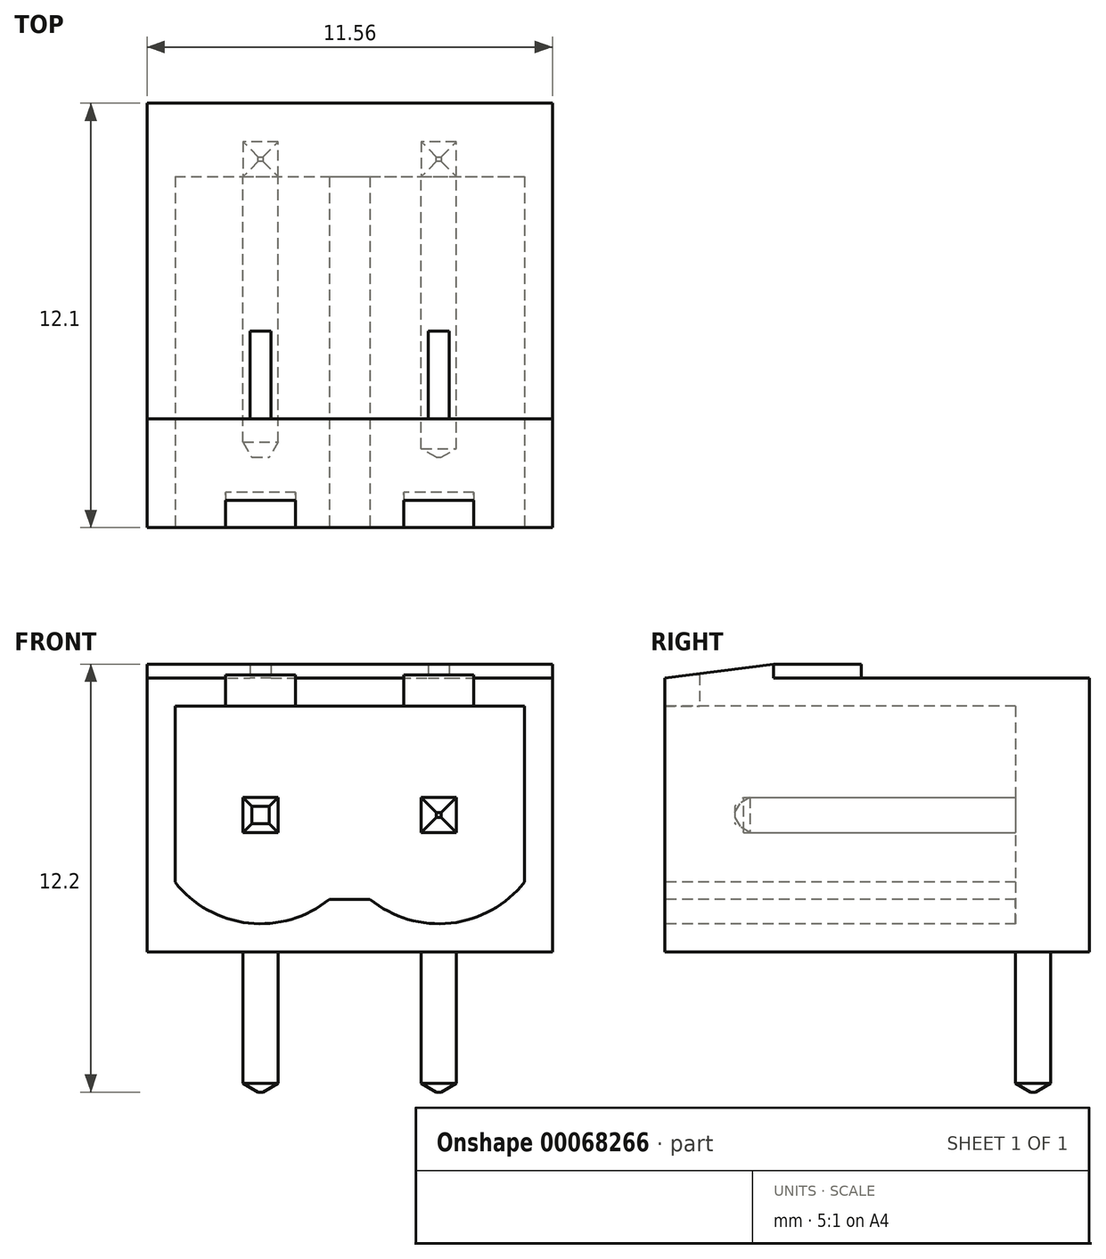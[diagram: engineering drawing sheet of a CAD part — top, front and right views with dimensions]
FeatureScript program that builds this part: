
annotation { "Feature Type Name" : "Feature", "Feature Type Description" : "" }
export const myFeature = defineFeature(function(context is Context, id is Id, definition is map)
    precondition{}
    {
        {
            var Q0;
            Q0=qCreatedBy(makeId("Top.planeOp"),FACE);
            var sketch = newSketch(context, id + "F0", { "sketchPlane" : qUnion([Q0])});
            skLineSegment(sketch, "E0.bottom", {"start": v(-5.78, 6.05) * mm, "end": v(5.78, 6.05) * mm});
            skLineSegment(sketch, "E0.top", {"start": v(-5.78, -6.05) * mm, "end": v(5.78, -6.05) * mm});
            skLineSegment(sketch, "E0.left", {"start": v(-5.78, 6.05) * mm, "end": v(-5.78, -6.05) * mm});
            skLineSegment(sketch, "E0.right", {"start": v(5.78, 6.05) * mm, "end": v(5.78, -6.05) * mm});
            skPoint(sketch, "E0.middle", {"position": v(0, 0) * mm});
            skSolve(sketch);
        }
        {
            var Q0;
            Q0=qSketchRegion(id+"F0",true);
            extrude(context, id + "F1", {"entities" : qUnion([Q0]), "depth" : 8.2 * mm});
        }
        {
            var Q0;
            Q0=makeQuery(id+"F1.opExtrude","SWEPT_FACE",FACE,{"disambiguationData":[OSD([sQuery(id+"F0.wireOp",EDGE,"E0.top")])]});
            var sketch = newSketch(context, id + "F2", { "sketchPlane" : qUnion([Q0])});
            skLineSegment(sketch, "E1.bottom", {"start": v(-4.98, 7) * mm, "end": v(4.98, 7) * mm});
            skLineSegment(sketch, "E1.top", {"start": v(-2.54, 0.8) * mm, "end": v(2.54, 0.8) * mm, "construction": true});
            skLineSegment(sketch, "E1.left", {"start": v(-4.98, 7) * mm, "end": v(-4.98, 1.99) * mm});
            skLineSegment(sketch, "E1.right", {"start": v(4.98, 7) * mm, "end": v(4.98, 1.99) * mm});
            skPoint(sketch, "E1.middle", {"position": v(0, 4.1) * mm});
            skPoint(sketch, "E1.middle.positionSnap0", {"position": v(0, 8.2) * mm});
            skPoint(sketch, "E1.middle.positionSnap1", {"position": v(-5.78, 4.1) * mm});
            skPoint(sketch, "E1.centerSnap0", {"position": v(0, 8.2) * mm});
            skPoint(sketch, "E1.centerSnap1", {"position": v(-5.78, 4.1) * mm});
            skArc(sketch, "E2", {"start": v(-4.98, 1.99) * mm, "mid": v(-2.88, 0.82) * mm, "end": v(-0.58, 1.5) * mm});
            skPoint(sketch, "E2.centerSnap0", {"position": v(-4.98, 3.9) * mm});
            skArc(sketch, "E3", {"start": v(0.58, 1.5) * mm, "mid": v(2.88, 0.82) * mm, "end": v(4.98, 1.99) * mm});
            skPoint(sketch, "E3.centerSnap0", {"position": v(4.98, 3.9) * mm});
            skLineSegment(sketch, "E4", {"start": v(-2.54, 3.9) * mm, "end": v(2.54, 3.9) * mm, "construction": true});
            skLineSegment(sketch, "E5", {"start": v(0, 3.9) * mm, "end": v(0, 7) * mm, "construction": true});
            skPoint(sketch, "E6.orphan", {"position": v(-4.98, 0.8) * mm});
            skPoint(sketch, "E7.orphan", {"position": v(4.98, 0.8) * mm});
            skLineSegment(sketch, "E8", {"start": v(-0.58, 1.5) * mm, "end": v(0.58, 1.5) * mm});
            skSolve(sketch);
        }
        {
            var Q0;
            Q0=qSketchRegion(id+"F2",true);
            extrude(context, id + "F3", {"entities" : qUnion([Q0]), "operationType" : NewBodyOperationType.REMOVE, "oppositeDirection" : true, "depth" : 10 * mm});
        }
        {
            var Q0;
            Q0=makeQuery(id+"F3.boolean.opBoolean","COPY",FACE,{"derivedFrom":makeQuery(id+"F3.opExtrude","CAP_FACE",FACE,{"disambiguationData":[OSD([sQuery(id+"F2.wireOp",EDGE,"E1.bottom"),sQuery(id+"F2.wireOp",EDGE,"E1.left"),sQuery(id+"F2.wireOp",EDGE,"E1.right"),sQuery(id+"F2.wireOp",EDGE,"E2"),sQuery(id+"F2.wireOp",EDGE,"E3"),sQuery(id+"F2.wireOp",EDGE,"E8")])],"isStart":false})});
            var sketch = newSketch(context, id + "F4", { "sketchPlane" : qUnion([Q0])});
            skLineSegment(sketch, "E9.bottom", {"start": v(-2.04, 4.4) * mm, "end": v(-3.04, 4.4) * mm});
            skLineSegment(sketch, "E9.top", {"start": v(-2.04, 3.4) * mm, "end": v(-3.04, 3.4) * mm});
            skLineSegment(sketch, "E9.left", {"start": v(-2.04, 4.4) * mm, "end": v(-2.04, 3.4) * mm});
            skLineSegment(sketch, "E9.right", {"start": v(-3.04, 4.4) * mm, "end": v(-3.04, 3.4) * mm});
            skPoint(sketch, "E9.middle", {"position": v(-2.54, 3.9) * mm});
            skLineSegment(sketch, "E10.bottom", {"start": v(2.04, 4.4) * mm, "end": v(3.04, 4.4) * mm});
            skLineSegment(sketch, "E10.top", {"start": v(2.04, 3.4) * mm, "end": v(3.04, 3.4) * mm});
            skLineSegment(sketch, "E10.left", {"start": v(2.04, 4.4) * mm, "end": v(2.04, 3.4) * mm});
            skLineSegment(sketch, "E10.right", {"start": v(3.04, 4.4) * mm, "end": v(3.04, 3.4) * mm});
            skPoint(sketch, "E10.middle", {"position": v(2.54, 3.9) * mm});
            skSolve(sketch);
        }
        {
            var Q0;
            Q0=qSketchRegion(id+"F4",true);
            extrude(context, id + "F5", {"entities" : qUnion([Q0]), "depth" : 8 * mm});
        }
        {
            var Q0;
            Q0=makeQuery(id+"F1.opExtrude","CAP_FACE",FACE,{"disambiguationData":[OSD([sQuery(id+"F0.wireOp",EDGE,"E0.bottom"),sQuery(id+"F0.wireOp",EDGE,"E0.top"),sQuery(id+"F0.wireOp",EDGE,"E0.left"),sQuery(id+"F0.wireOp",EDGE,"E0.right")])],"isStart":true});
            var sketch = newSketch(context, id + "F6", { "sketchPlane" : qUnion([Q0])});
            skPoint(sketch, "E11.centerSnap0", {"position": v(-5.78, 0) * mm});
            skPoint(sketch, "E12.centerSnap0", {"position": v(5.78, 0) * mm});
            skLineSegment(sketch, "E13", {"start": v(-2.54, -4.45) * mm, "end": v(2.54, -4.45) * mm, "construction": true});
            skLineSegment(sketch, "E14", {"start": v(0, -4.45) * mm, "end": v(0, -6.05) * mm, "construction": true});
            skLineSegment(sketch, "E15.bottom", {"start": v(-3.04, -3.95) * mm, "end": v(-2.04, -3.95) * mm});
            skLineSegment(sketch, "E15.top", {"start": v(-3.04, -4.95) * mm, "end": v(-2.04, -4.95) * mm});
            skLineSegment(sketch, "E15.left", {"start": v(-3.04, -3.95) * mm, "end": v(-3.04, -4.95) * mm});
            skLineSegment(sketch, "E15.right", {"start": v(-2.04, -3.95) * mm, "end": v(-2.04, -4.95) * mm});
            skPoint(sketch, "E15.middle", {"position": v(-2.54, -4.45) * mm});
            skLineSegment(sketch, "E16.bottom", {"start": v(2.04, -3.95) * mm, "end": v(3.04, -3.95) * mm});
            skLineSegment(sketch, "E16.top", {"start": v(2.04, -4.95) * mm, "end": v(3.04, -4.95) * mm});
            skLineSegment(sketch, "E16.left", {"start": v(2.04, -3.95) * mm, "end": v(2.04, -4.95) * mm});
            skLineSegment(sketch, "E16.right", {"start": v(3.04, -3.95) * mm, "end": v(3.04, -4.95) * mm});
            skPoint(sketch, "E16.middle", {"position": v(2.54, -4.45) * mm});
            skSolve(sketch);
        }
        {
            var Q0;
            Q0=qSketchRegion(id+"F6",true);
            extrude(context, id + "F7", {"entities" : qUnion([Q0]), "depth" : 4 * mm});
        }
        {
            var Q0;
            Q0=makeQuery(id+"F1.opExtrude","SWEPT_FACE",FACE,{"disambiguationData":[OSD([sQuery(id+"F0.wireOp",EDGE,"E0.right")])]});
            var sketch = newSketch(context, id + "F8", { "sketchPlane" : qUnion([Q0])});
            skLineSegment(sketch, "E17.bottom", {"start": v(6.05, 8.2) * mm, "end": v(-2.95, 8.2) * mm});
            skLineSegment(sketch, "E17.top", {"start": v(6.05, 7.8) * mm, "end": v(-2.95, 7.8) * mm});
            skLineSegment(sketch, "E17.left", {"start": v(6.05, 8.2) * mm, "end": v(6.05, 7.8) * mm});
            skLineSegment(sketch, "E17.right", {"start": v(-2.95, 8.2) * mm, "end": v(-2.95, 7.8) * mm});
            skLineSegment(sketch, "E18", {"start": v(-6.05, 7.8) * mm, "end": v(-2.95, 8.2) * mm});
            skLineSegment(sketch, "E19", {"start": v(-6.05, 8.2) * mm, "end": v(-6.05, 7.8) * mm});
            skLineSegment(sketch, "E20", {"start": v(-6.05, 8.2) * mm, "end": v(-2.95, 8.2) * mm});
            skSolve(sketch);
        }
        {
            var Q0;
            Q0=qSketchRegion(id+"F8",true);
            extrude(context, id + "F9", {"entities" : qUnion([Q0]), "operationType" : NewBodyOperationType.REMOVE, "oppositeDirection" : true, "depth" : 25 * mm});
        }
        {
            var Q0;
            Q0=makeQuery(id+"F5.opExtrude","CAP_FACE",FACE,{"disambiguationData":[OSD([sQuery(id+"F4.wireOp",EDGE,"E10.bottom"),sQuery(id+"F4.wireOp",EDGE,"E10.top"),sQuery(id+"F4.wireOp",EDGE,"E10.left"),sQuery(id+"F4.wireOp",EDGE,"E10.right")])],"isStart":false});
            var Q1;
            Q1=makeQuery(id+"F5.opExtrude","CAP_FACE",FACE,{"disambiguationData":[OSD([sQuery(id+"F4.wireOp",EDGE,"E9.bottom"),sQuery(id+"F4.wireOp",EDGE,"E9.top"),sQuery(id+"F4.wireOp",EDGE,"E9.left"),sQuery(id+"F4.wireOp",EDGE,"E9.right")])],"isStart":false});
            var Q2;
            Q2=makeQuery(id+"F7.opExtrude","CAP_FACE",FACE,{"disambiguationData":[OSD([sQuery(id+"F6.wireOp",EDGE,"E16.bottom"),sQuery(id+"F6.wireOp",EDGE,"E16.top"),sQuery(id+"F6.wireOp",EDGE,"E16.left"),sQuery(id+"F6.wireOp",EDGE,"E16.right")])],"isStart":false});
            var Q3;
            Q3=makeQuery(id+"F7.opExtrude","CAP_FACE",FACE,{"disambiguationData":[OSD([sQuery(id+"F6.wireOp",EDGE,"E15.bottom"),sQuery(id+"F6.wireOp",EDGE,"E15.top"),sQuery(id+"F6.wireOp",EDGE,"E15.left"),sQuery(id+"F6.wireOp",EDGE,"E15.right")])],"isStart":false});
            chamfer(context, id + "F10", {"entities" : qUnion([Q0, Q1, Q2, Q3]), "chamferType" : ChamferType.OFFSET_ANGLE, "width" : 0.25 * mm, "oppositeDirection" : false, "angle" : 60 * degree, "tangentPropagation" : true});
        }
        {
            var Q0;
            Q0=makeQuery(id+"F1.opExtrude","SWEPT_FACE",FACE,{"disambiguationData":[OSD([sQuery(id+"F0.wireOp",EDGE,"E0.top")])]});
            var sketch = newSketch(context, id + "F11", { "sketchPlane" : qUnion([Q0])});
            skLineSegment(sketch, "E21.bottom", {"start": v(-1.54, 7.9) * mm, "end": v(-3.54, 7.9) * mm});
            skLineSegment(sketch, "E21.top", {"start": v(-1.54, 6.9) * mm, "end": v(-3.54, 6.9) * mm});
            skLineSegment(sketch, "E21.left", {"start": v(-1.54, 7.9) * mm, "end": v(-1.54, 6.9) * mm});
            skLineSegment(sketch, "E21.right", {"start": v(-3.54, 7.9) * mm, "end": v(-3.54, 6.9) * mm});
            skPoint(sketch, "E21.middle", {"position": v(-2.54, 7.4) * mm});
            skLineSegment(sketch, "E22", {"start": v(-2.54, 3.9) * mm, "end": v(-2.54, 7.8) * mm, "construction": true});
            skLineSegment(sketch, "E23.bottom", {"start": v(3.54, 7.9) * mm, "end": v(1.54, 7.9) * mm});
            skLineSegment(sketch, "E23.top", {"start": v(3.54, 6.9) * mm, "end": v(1.54, 6.9) * mm});
            skLineSegment(sketch, "E23.left", {"start": v(3.54, 7.9) * mm, "end": v(3.54, 6.9) * mm});
            skLineSegment(sketch, "E23.right", {"start": v(1.54, 7.9) * mm, "end": v(1.54, 6.9) * mm});
            skPoint(sketch, "E23.middle", {"position": v(2.54, 7.4) * mm});
            skSolve(sketch);
        }
        {
            var Q0;
            Q0=qSketchRegion(id+"F11",true);
            extrude(context, id + "F12", {"entities" : qUnion([Q0]), "operationType" : NewBodyOperationType.REMOVE, "oppositeDirection" : true, "depth" : 1 * mm});
        }
        {
            var Q0;
            Q0=makeQuery(id+"F9.boolean.opBoolean","COPY",FACE,{"derivedFrom":makeQuery(id+"F9.opExtrude","SWEPT_FACE",FACE,{"disambiguationData":[OSD([sQuery(id+"F8.wireOp",EDGE,"E17.top")])]})});
            var sketch = newSketch(context, id + "F13", { "sketchPlane" : qUnion([Q0])});
            skLineSegment(sketch, "E24.bottom", {"start": v(-2.24, -2.95) * mm, "end": v(-2.84, -2.95) * mm});
            skLineSegment(sketch, "E24.top", {"start": v(-2.24, -0.45) * mm, "end": v(-2.84, -0.45) * mm});
            skLineSegment(sketch, "E24.left", {"start": v(-2.24, -2.95) * mm, "end": v(-2.24, -0.45) * mm});
            skLineSegment(sketch, "E24.right", {"start": v(-2.84, -2.95) * mm, "end": v(-2.84, -0.45) * mm});
            skPoint(sketch, "E24.middle", {"position": v(-2.54, -1.7) * mm});
            skLineSegment(sketch, "E25", {"start": v(-2.54, -2.95) * mm, "end": v(-2.54, -5.27) * mm, "construction": true});
            skPoint(sketch, "E25.endSnap0", {"position": v(-2.54, -2.95) * mm});
            skLineSegment(sketch, "E26.bottom", {"start": v(2.24, -0.45) * mm, "end": v(2.84, -0.45) * mm});
            skLineSegment(sketch, "E26.top", {"start": v(2.24, -2.95) * mm, "end": v(2.84, -2.95) * mm});
            skLineSegment(sketch, "E26.left", {"start": v(2.24, -0.45) * mm, "end": v(2.24, -2.95) * mm});
            skLineSegment(sketch, "E26.right", {"start": v(2.84, -0.45) * mm, "end": v(2.84, -2.95) * mm});
            skPoint(sketch, "E26.middle", {"position": v(2.54, -1.7) * mm});
            skSolve(sketch);
        }
        {
            var Q0;
            Q0=qSketchRegion(id+"F13",true);
            extrude(context, id + "F14", {"entities" : qUnion([Q0]), "operationType" : NewBodyOperationType.ADD, "depth" : 0.4 * mm});
        }
    });
